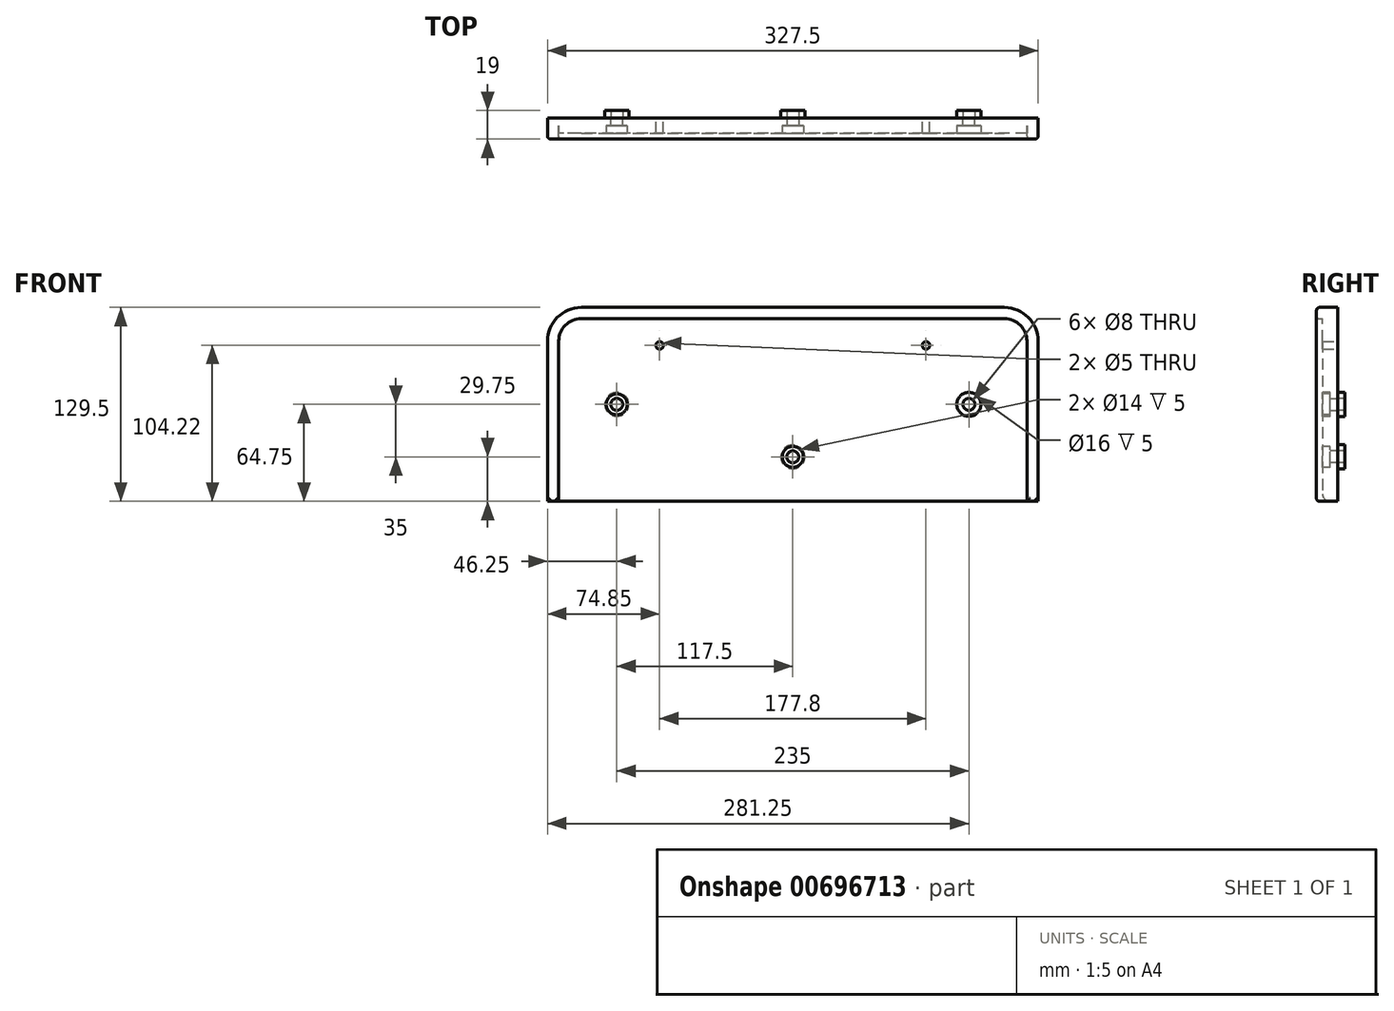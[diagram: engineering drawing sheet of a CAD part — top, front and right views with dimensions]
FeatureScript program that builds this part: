
annotation { "Feature Type Name" : "Feature", "Feature Type Description" : "" }
export const myFeature = defineFeature(function(context is Context, id is Id, definition is map)
    precondition{}
    {
        {
            var Q0;
            Q0=qCreatedBy(makeId("Front.planeOp"),FACE);
            var sketch = newSketch(context, id + "F0", { "sketchPlane" : qUnion([Q0])});
            skLineSegment(sketch, "E0.top", {"start": v(141.25, 57.25) * mm, "end": v(-141.25, 57.25) * mm});
            skLineSegment(sketch, "E0.left", {"start": v(156.25, -64.75) * mm, "end": v(156.25, 42.25) * mm});
            skLineSegment(sketch, "E0.right", {"start": v(-156.25, -64.75) * mm, "end": v(-156.25, 42.25) * mm});
            skPoint(sketch, "E0.middle", {"position": v(0, 0) * mm});
            skPoint(sketch, "E1.visualSharp", {"position": v(-156.25, 57.25) * mm});
            skArc(sketch, "E1.filletArc", {"start": v(-141.25, 57.25) * mm, "mid": v(-151.86, 52.86) * mm, "end": v(-156.25, 42.25) * mm});
            skPoint(sketch, "E2.visualSharp", {"position": v(156.25, 57.25) * mm});
            skArc(sketch, "E2.filletArc", {"start": v(156.25, 42.25) * mm, "mid": v(151.86, 52.86) * mm, "end": v(141.25, 57.25) * mm});
            skLineSegment(sketch, "E3", {"start": v(-156.25, 39.47) * mm, "end": v(156.25, 39.47) * mm, "construction": true});
            skCircle(sketch, "E4", {"center": v(-88.9, 39.47) * mm, "radius": 2.5 * mm});
            skCircle(sketch, "E5", {"center": v(88.9, 39.47) * mm, "radius": 2.5 * mm});
            skArc(sketch, "E6.0", {"start": v(163.75, 42.25) * mm, "mid": v(157.16, 58.16) * mm, "end": v(141.25, 64.75) * mm});
            skArc(sketch, "E6.1", {"start": v(-141.25, 64.75) * mm, "mid": v(-157.16, 58.16) * mm, "end": v(-163.75, 42.25) * mm});
            skLineSegment(sketch, "E6.2", {"start": v(-163.75, -64.75) * mm, "end": v(-163.75, 42.25) * mm});
            skLineSegment(sketch, "E6.3", {"start": v(141.25, 64.75) * mm, "end": v(-141.25, 64.75) * mm});
            skLineSegment(sketch, "E6.4", {"start": v(163.75, -64.75) * mm, "end": v(-163.75, -64.75) * mm});
            skLineSegment(sketch, "E6.5", {"start": v(163.75, -64.75) * mm, "end": v(163.75, 42.25) * mm});
            skLineSegment(sketch, "E7", {"start": v(-156.25, 0) * mm, "end": v(156.25, 0) * mm, "construction": true});
            skCircle(sketch, "E8", {"center": v(-117.5, 0) * mm, "radius": 4 * mm});
            skCircle(sketch, "E9", {"center": v(117.5, 0) * mm, "radius": 4 * mm});
            skSolve(sketch);
        }
        {
            var Q0;
            Q0=makeQuery(id+"F0.imprint","IMPRINT",FACE,{"disambiguationData":[TD([[makeQuery(id+"F0.imprint","IMPRINT",EDGE,{"derivedFrom":sQuery(id+"F0.wireOp",EDGE,"E0.top")}),-1.0]])]});
            var Q1;
            Q1=makeQuery(id+"F0.imprint","IMPRINT",FACE,{"disambiguationData":[TD([[makeQuery(id+"F0.imprint","IMPRINT",EDGE,{"derivedFrom":sQuery(id+"F0.wireOp",EDGE,"E0.top")}),1.0]])]});
            extrude(context, id + "F1", {"entities" : qUnion([Q0, Q1]), "depth" : 10 * mm, "offsetDistance" : 25 * mm});
        }
        {
            var Q0;
            Q0=makeQuery(id+"F0.imprint","IMPRINT",FACE,{"disambiguationData":[TD([[makeQuery(id+"F0.imprint","IMPRINT",EDGE,{"derivedFrom":sQuery(id+"F0.wireOp",EDGE,"E0.top")}),-1.0]])]});
            extrude(context, id + "F2", {"entities" : qUnion([Q0]), "operationType" : NewBodyOperationType.ADD, "depth" : 14 * mm, "offsetDistance" : 25 * mm});
        }
        {
            var Q0;
            Q0=makeQuery(id+"F2.opExtrude","CAP_EDGE",EDGE,{"disambiguationData":[OSD([sQuery(id+"F0.wireOp",EDGE,"E6.2")])],"isStart":false});
            var Q1;
            Q1=makeQuery(id+"F2.opExtrude","CAP_EDGE",EDGE,{"disambiguationData":[OSD([sQuery(id+"F0.wireOp",EDGE,"E0.top")])],"isStart":false});
            var Q2;
            {var subQ0=sQuery(id+"F0.wireOp",EDGE,"E6.4");Q2=makeQuery(id+"F2.opExtrude","CAP_EDGE",EDGE,{"disambiguationData":[OSD([subQ0]),TDD([makeQuery(id+"F0.imprint","IMPRINT",EDGE,{"disambiguationData":[TD([[makeQuery(id+"F0.imprint","INTERSECT",VERTEX,{"derivedFrom":[sQuery(id+"F0.wireOp",EDGE,"E0.right"),subQ0]}),-1.0]])],"derivedFrom":subQ0})])],"isStart":false});}
            var Q3;
            {var subQ0=sQuery(id+"F0.wireOp",EDGE,"E6.4");Q3=makeQuery(id+"F2.opExtrude","CAP_EDGE",EDGE,{"disambiguationData":[OSD([subQ0]),TDD([makeQuery(id+"F0.imprint","IMPRINT",EDGE,{"disambiguationData":[TD([[makeQuery(id+"F0.imprint","INTERSECT",VERTEX,{"derivedFrom":[sQuery(id+"F0.wireOp",EDGE,"E0.left"),subQ0]}),1.0]])],"derivedFrom":subQ0})])],"isStart":false});}
            fillet(context, id + "F3", {"entities" : qUnion([Q0, Q1, Q2, Q3]), "radius" : 2 * mm, "tangentPropagation" : true, "allowEdgeOverflow" : false});
        }
        {
            var Q0;
            Q0=makeQuery(id+"F1.opExtrude","CAP_EDGE",EDGE,{"disambiguationData":[OSD([sQuery(id+"F0.wireOp",EDGE,"E6.4")])],"isStart":false});
            fillet(context, id + "F4", {"entities" : qUnion([Q0]), "radius" : 5 * mm, "tangentPropagation" : true, "allowEdgeOverflow" : false});
        }
        {
            var Q0;
            Q0=makeQuery(id+"F1.opExtrude","CAP_FACE",FACE,{"disambiguationData":[OSD([sQuery(id+"F0.wireOp",EDGE,"E4"),sQuery(id+"F0.wireOp",EDGE,"E5"),sQuery(id+"F0.wireOp",EDGE,"E6.0"),sQuery(id+"F0.wireOp",EDGE,"E6.1"),sQuery(id+"F0.wireOp",EDGE,"E6.2"),sQuery(id+"F0.wireOp",EDGE,"E6.3"),sQuery(id+"F0.wireOp",EDGE,"E6.4"),sQuery(id+"F0.wireOp",EDGE,"E6.5"),sQuery(id+"F0.wireOp",EDGE,"E8"),sQuery(id+"F0.wireOp",EDGE,"E9")])],"isStart":false});
            var sketch = newSketch(context, id + "F5", { "sketchPlane" : qUnion([Q0])});
            skCircle(sketch, "E10", {"center": v(-117.5, 0) * mm, "radius": 7 * mm});
            skCircle(sketch, "E11", {"center": v(117.5, 0) * mm, "radius": 8 * mm});
            skSolve(sketch);
        }
        {
            var Q0;
            Q0 = qSketchRegion(id + "F5", true);
            extrude(context, id + "F6", {"entities" : qUnion([Q0]), "operationType" : NewBodyOperationType.REMOVE, "oppositeDirection" : true, "depth" : 5 * mm, "offsetDistance" : 25 * mm});
        }
        {
            var Q0;
            Q0=makeQuery(id+"F0.imprint","IMPRINT",FACE,{"disambiguationData":[TD([[makeQuery(id+"F0.imprint","IMPRINT",EDGE,{"derivedFrom":sQuery(id+"F0.wireOp",EDGE,"E0.top")}),1.0]])]});
            var sketch = newSketch(context, id + "F7", { "sketchPlane" : qUnion([Q0])});
            skCircle(sketch, "E12", {"center": v(117.5, 0) * mm, "radius": 8 * mm});
            skCircle(sketch, "E13", {"center": v(-117.5, 0) * mm, "radius": 8 * mm});
            skCircle(sketch, "E14", {"center": v(117.5, 0) * mm, "radius": 4 * mm});
            skCircle(sketch, "E15", {"center": v(-117.5, 0) * mm, "radius": 4 * mm});
            skCircle(sketch, "E16", {"center": v(0, -35) * mm, "radius": 4 * mm});
            skCircle(sketch, "E17", {"center": v(0, -35) * mm, "radius": 8 * mm});
            skSolve(sketch);
        }
        {
            var Q0;
            Q0 = qSketchRegion(id + "F7", true);
            extrude(context, id + "F8", {"entities" : qUnion([Q0]), "oppositeDirection" : true, "depth" : 5 * mm, "offsetDistance" : 25 * mm});
        }
        {
            var Q0;
            Q0=makeQuery(id+"F1.opExtrude","CAP_FACE",FACE,{"disambiguationData":[OSD([sQuery(id+"F0.wireOp",EDGE,"E4"),sQuery(id+"F0.wireOp",EDGE,"E5"),sQuery(id+"F0.wireOp",EDGE,"E6.0"),sQuery(id+"F0.wireOp",EDGE,"E6.1"),sQuery(id+"F0.wireOp",EDGE,"E6.2"),sQuery(id+"F0.wireOp",EDGE,"E6.3"),sQuery(id+"F0.wireOp",EDGE,"E6.4"),sQuery(id+"F0.wireOp",EDGE,"E6.5"),sQuery(id+"F0.wireOp",EDGE,"E8"),sQuery(id+"F0.wireOp",EDGE,"E9")])],"isStart":false});
            var sketch = newSketch(context, id + "F9", { "sketchPlane" : qUnion([Q0])});
            skCircle(sketch, "E18", {"center": v(0, -35) * mm, "radius": 4 * mm});
            skSolve(sketch);
        }
        {
            var Q0;
            Q0=makeQuery(id+"F9.imprint","IMPRINT",FACE,{"disambiguationData":[TD([[makeQuery(id+"F9.imprint","IMPRINT",EDGE,{"derivedFrom":sQuery(id+"F9.wireOp",EDGE,"E18")}),1.0]])]});
            extrude(context, id + "F10", {"entities" : qUnion([Q0]), "operationType" : NewBodyOperationType.REMOVE, "oppositeDirection" : true, "depth" : 25 * mm, "offsetDistance" : 25 * mm});
        }
        {
            var Q0;
            Q0=makeQuery(id+"F1.opExtrude","CAP_FACE",FACE,{"disambiguationData":[OSD([sQuery(id+"F0.wireOp",EDGE,"E4"),sQuery(id+"F0.wireOp",EDGE,"E5"),sQuery(id+"F0.wireOp",EDGE,"E6.0"),sQuery(id+"F0.wireOp",EDGE,"E6.1"),sQuery(id+"F0.wireOp",EDGE,"E6.2"),sQuery(id+"F0.wireOp",EDGE,"E6.3"),sQuery(id+"F0.wireOp",EDGE,"E6.4"),sQuery(id+"F0.wireOp",EDGE,"E6.5"),sQuery(id+"F0.wireOp",EDGE,"E8"),sQuery(id+"F0.wireOp",EDGE,"E9")])],"isStart":false});
            var sketch = newSketch(context, id + "F11", { "sketchPlane" : qUnion([Q0])});
            skCircle(sketch, "E19", {"center": v(0, -35) * mm, "radius": 7 * mm});
            skSolve(sketch);
        }
        {
            var Q0;
            Q0=makeQuery(id+"F11.imprint","IMPRINT",FACE,{"disambiguationData":[TD([[makeQuery(id+"F11.imprint","IMPRINT",EDGE,{"derivedFrom":sQuery(id+"F11.wireOp",EDGE,"E19")}),1.0]])]});
            extrude(context, id + "F12", {"entities" : qUnion([Q0]), "operationType" : NewBodyOperationType.REMOVE, "oppositeDirection" : true, "depth" : 5 * mm, "offsetDistance" : 25 * mm});
        }
    });
